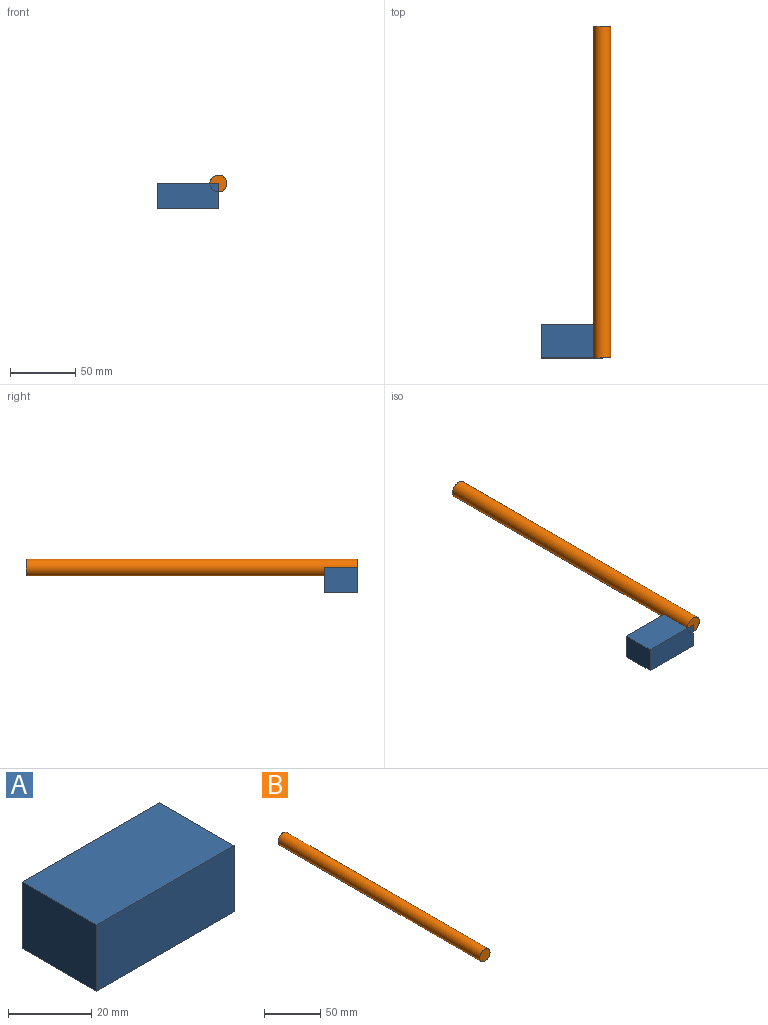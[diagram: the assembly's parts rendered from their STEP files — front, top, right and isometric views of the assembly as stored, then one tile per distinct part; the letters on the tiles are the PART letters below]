
ASSEMBLY  parts=2 mates=1
PART A: 6 faces, bbox 46.8x25.4x19.5 mm
  f0: plane 25.4x19.54mm, normal (-1,0,0), area 496.4mm2, adj f1,f3,f4,f5
  f1: plane 46.83x25.4mm, normal (0,0,-1), area 1189.4mm2, adj f0,f2,f4,f5
  f2: plane 25.4x19.54mm, normal (1,0,0), area 496.4mm2, adj f1,f3,f4,f5
  f3: plane 46.83x25.4mm, normal (0,0,1), area 1189.4mm2, adj f0,f2,f4,f5
  f4: plane 46.83x19.54mm, normal (0,-1,0), area 915.1mm2, adj f0,f1,f2,f3
  f5: plane 46.83x19.54mm, normal (0,1,0), area 915.1mm2, adj f0,f1,f2,f3
PART B: 3 faces, bbox 12.9x254x12.9 mm
  f0: cylinder r=6.46mm len=254mm, axis (0,1,0), area 10314.4mm2, adj f1,f2
  f1: plane 12.93x12.93mm, normal (0,-1,0), area 131.2mm2, adj f0
  f2: plane 12.93x12.93mm, normal (0,1,0), area 131.2mm2, adj f0
PLACE A t=(-35.64,-170.47,-150.89)mm
PLACE B t=(29.07,58.13,-96.5)mm
MATE fastened B.f0 <-> A.f4  axis (0,-1,0) through (29.07,-195.87,-96.5)mm
